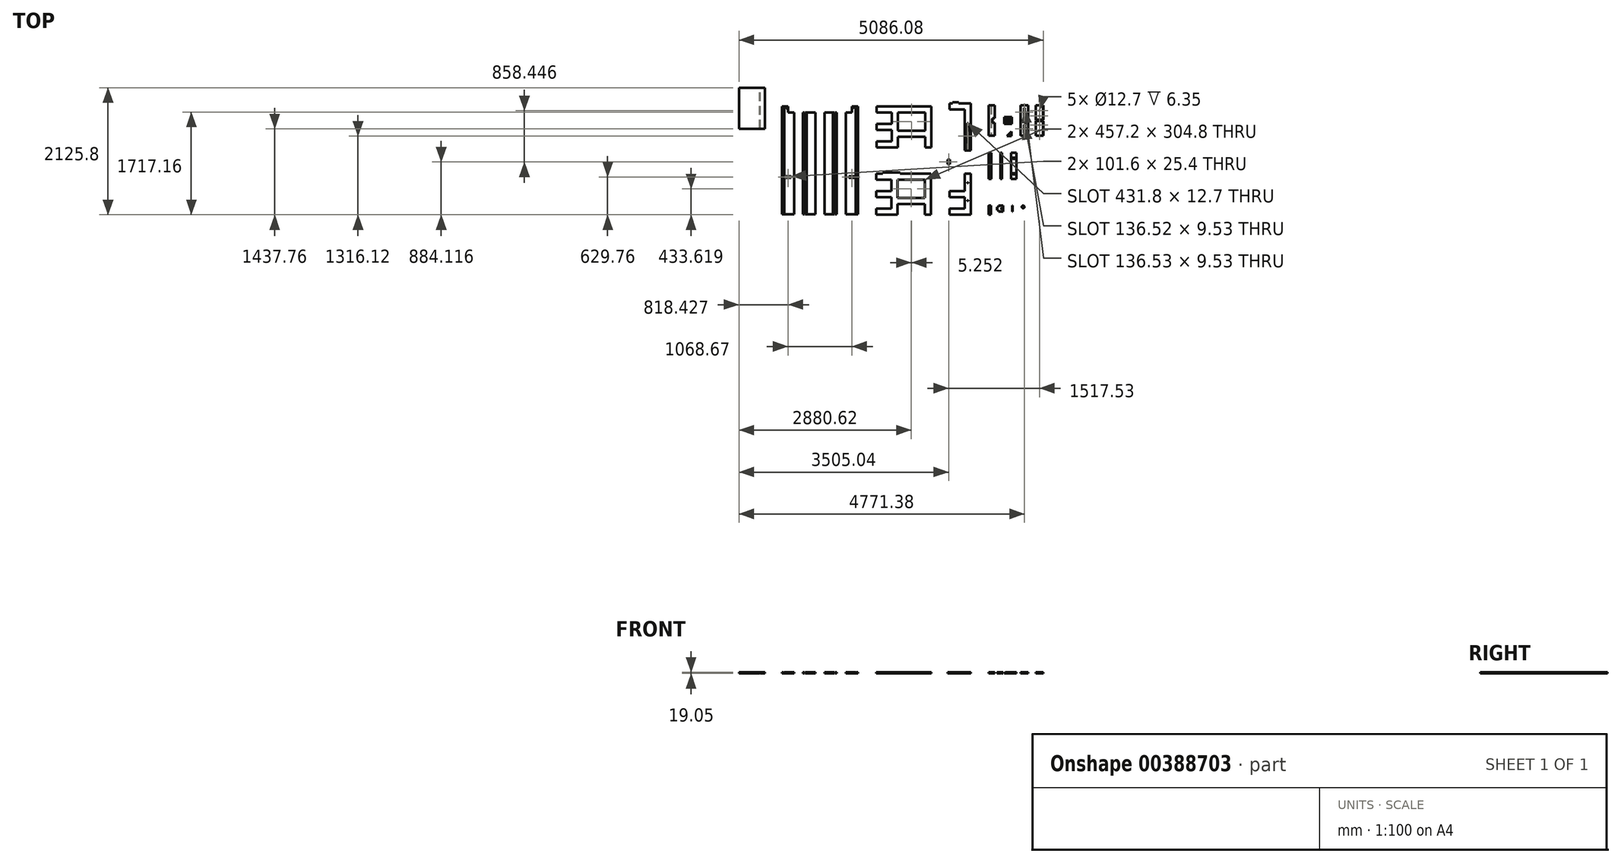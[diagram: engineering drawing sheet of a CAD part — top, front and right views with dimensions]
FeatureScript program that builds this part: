
annotation { "Feature Type Name" : "Feature", "Feature Type Description" : "" }
export const myFeature = defineFeature(function(context is Context, id is Id, definition is map)
    precondition{}
    {
        {
            var Q0;
            Q0=qCreatedBy(makeId("Top.planeOp"),FACE);
            var sketch = newSketch(context, id + "F0", { "sketchPlane" : qUnion([Q0])});
            skLineSegment(sketch, "E0.bottom", {"start": v(-431.8, 0) * mm, "end": v(0, 0) * mm});
            skLineSegment(sketch, "E0.top", {"start": v(-431.8, -685.8) * mm, "end": v(0, -685.8) * mm});
            skLineSegment(sketch, "E0.left", {"start": v(-431.8, 0) * mm, "end": v(-431.8, -685.8) * mm});
            skLineSegment(sketch, "E0.right", {"start": v(0, 0) * mm, "end": v(0, -685.8) * mm});
            skLineSegment(sketch, "E1", {"start": v(1869.87, -315.68) * mm, "end": v(2784.27, -315.68) * mm});
            skLineSegment(sketch, "E2", {"start": v(2784.27, -315.68) * mm, "end": v(2784.27, -1001.48) * mm});
            skLineSegment(sketch, "E3", {"start": v(2784.27, -1001.48) * mm, "end": v(2682.67, -1001.48) * mm});
            skLineSegment(sketch, "E4", {"start": v(2682.67, -1001.48) * mm, "end": v(2682.67, -823.68) * mm});
            skLineSegment(sketch, "E5", {"start": v(2682.67, -823.68) * mm, "end": v(2225.47, -823.68) * mm});
            skLineSegment(sketch, "E6", {"start": v(2225.47, -823.68) * mm, "end": v(2225.47, -1001.48) * mm});
            skLineSegment(sketch, "E7", {"start": v(2225.47, -1001.48) * mm, "end": v(1869.87, -1001.48) * mm});
            skLineSegment(sketch, "E8", {"start": v(1869.87, -1001.48) * mm, "end": v(1869.87, -899.88) * mm});
            skLineSegment(sketch, "E9", {"start": v(1869.87, -899.88) * mm, "end": v(2123.87, -899.88) * mm});
            skLineSegment(sketch, "E10", {"start": v(2123.87, -899.88) * mm, "end": v(2123.87, -709.38) * mm});
            skLineSegment(sketch, "E11", {"start": v(2123.87, -709.38) * mm, "end": v(1869.87, -709.38) * mm});
            skLineSegment(sketch, "E12", {"start": v(1869.87, -709.38) * mm, "end": v(1869.87, -607.78) * mm});
            skLineSegment(sketch, "E13", {"start": v(1869.87, -607.78) * mm, "end": v(2123.87, -607.78) * mm});
            skLineSegment(sketch, "E14", {"start": v(2123.87, -607.78) * mm, "end": v(2123.87, -417.28) * mm});
            skLineSegment(sketch, "E15", {"start": v(2123.87, -417.28) * mm, "end": v(1869.87, -417.28) * mm});
            skLineSegment(sketch, "E16", {"start": v(1869.87, -417.28) * mm, "end": v(1869.87, -315.68) * mm});
            skLineSegment(sketch, "E17.bottom", {"start": v(2225.47, -417.28) * mm, "end": v(2682.67, -417.28) * mm});
            skLineSegment(sketch, "E17.top", {"start": v(2225.47, -722.08) * mm, "end": v(2682.67, -722.08) * mm});
            skLineSegment(sketch, "E17.left", {"start": v(2225.47, -417.28) * mm, "end": v(2225.47, -722.08) * mm});
            skLineSegment(sketch, "E17.right", {"start": v(2682.67, -417.28) * mm, "end": v(2682.67, -722.08) * mm});
            skLineSegment(sketch, "E18", {"start": v(1864.62, -1438.18) * mm, "end": v(1972.57, -1438.18) * mm});
            skLineSegment(sketch, "E19", {"start": v(2779.02, -1438.18) * mm, "end": v(2779.02, -2123.98) * mm});
            skLineSegment(sketch, "E20", {"start": v(2779.02, -2123.98) * mm, "end": v(2677.42, -2123.98) * mm});
            skLineSegment(sketch, "E21", {"start": v(2677.42, -2123.98) * mm, "end": v(2677.42, -1946.18) * mm});
            skLineSegment(sketch, "E22", {"start": v(2677.42, -1946.18) * mm, "end": v(2220.22, -1946.18) * mm});
            skLineSegment(sketch, "E23", {"start": v(2220.22, -1946.18) * mm, "end": v(2220.22, -2123.98) * mm});
            skLineSegment(sketch, "E24", {"start": v(2220.22, -2123.98) * mm, "end": v(1864.62, -2123.98) * mm});
            skLineSegment(sketch, "E25", {"start": v(1864.62, -2123.98) * mm, "end": v(1864.62, -2022.38) * mm});
            skLineSegment(sketch, "E26", {"start": v(1864.62, -2022.38) * mm, "end": v(2118.62, -2022.38) * mm});
            skLineSegment(sketch, "E27", {"start": v(2118.62, -2022.38) * mm, "end": v(2118.62, -1831.88) * mm});
            skLineSegment(sketch, "E28", {"start": v(2118.62, -1831.88) * mm, "end": v(1864.62, -1831.88) * mm});
            skLineSegment(sketch, "E29", {"start": v(1864.62, -1831.88) * mm, "end": v(1864.62, -1730.28) * mm});
            skLineSegment(sketch, "E30", {"start": v(1864.62, -1730.28) * mm, "end": v(2118.62, -1730.28) * mm});
            skLineSegment(sketch, "E31", {"start": v(2118.62, -1730.28) * mm, "end": v(2118.62, -1539.78) * mm});
            skLineSegment(sketch, "E32", {"start": v(2118.62, -1539.78) * mm, "end": v(1864.62, -1539.78) * mm});
            skLineSegment(sketch, "E33", {"start": v(1864.62, -1539.78) * mm, "end": v(1864.62, -1438.18) * mm});
            skLineSegment(sketch, "E34.bottom", {"start": v(2220.22, -1539.78) * mm, "end": v(2677.42, -1539.78) * mm});
            skLineSegment(sketch, "E34.top", {"start": v(2220.22, -1844.58) * mm, "end": v(2677.42, -1844.58) * mm});
            skLineSegment(sketch, "E34.left", {"start": v(2220.22, -1539.78) * mm, "end": v(2220.22, -1844.58) * mm});
            skLineSegment(sketch, "E34.right", {"start": v(2677.42, -1539.78) * mm, "end": v(2677.42, -1844.58) * mm});
            skLineSegment(sketch, "E35", {"start": v(1972.57, -1438.18) * mm, "end": v(1972.57, -1419.13) * mm});
            skLineSegment(sketch, "E36", {"start": v(1972.57, -1419.13) * mm, "end": v(2264.67, -1419.13) * mm});
            skLineSegment(sketch, "E37", {"start": v(2264.67, -1419.13) * mm, "end": v(2264.67, -1438.18) * mm});
            skLineSegment(sketch, "E38.trimOffspring", {"start": v(2264.67, -1438.18) * mm, "end": v(2779.02, -1438.18) * mm});
            skLineSegment(sketch, "E39", {"start": v(3088.07, -263.58) * mm, "end": v(3138.87, -263.58) * mm});
            skLineSegment(sketch, "E40", {"start": v(3138.87, -263.58) * mm, "end": v(3138.87, -244.53) * mm});
            skLineSegment(sketch, "E41", {"start": v(3138.87, -244.53) * mm, "end": v(3240.47, -244.53) * mm});
            skLineSegment(sketch, "E42", {"start": v(3240.47, -244.53) * mm, "end": v(3240.47, -263.58) * mm});
            skLineSegment(sketch, "E43", {"start": v(3240.47, -263.58) * mm, "end": v(3443.67, -263.58) * mm});
            skLineSegment(sketch, "E44", {"start": v(3443.67, -263.58) * mm, "end": v(3443.67, -1050.98) * mm});
            skLineSegment(sketch, "E45", {"start": v(3443.67, -1050.98) * mm, "end": v(3342.07, -1050.98) * mm});
            skLineSegment(sketch, "E46", {"start": v(3342.07, -1050.98) * mm, "end": v(3342.07, -365.18) * mm});
            skLineSegment(sketch, "E47", {"start": v(3342.07, -365.18) * mm, "end": v(3088.07, -365.18) * mm});
            skLineSegment(sketch, "E48", {"start": v(3088.07, -365.18) * mm, "end": v(3088.07, -263.58) * mm});
            skLineSegment(sketch, "E49.bottom", {"start": v(3392.87, -593.78) * mm, "end": v(3392.87, -593.78) * mm});
            skLineSegment(sketch, "E49.top", {"start": v(3392.87, -1025.58) * mm, "end": v(3392.87, -1025.58) * mm});
            skLineSegment(sketch, "E49.left", {"start": v(3386.52, -600.13) * mm, "end": v(3386.52, -1019.23) * mm});
            skLineSegment(sketch, "E49.right", {"start": v(3399.22, -600.13) * mm, "end": v(3399.22, -1019.23) * mm});
            skLineSegment(sketch, "E50", {"start": v(3392.87, -593.78) * mm, "end": v(3392.87, -1025.58) * mm, "construction": true});
            skPoint(sketch, "E51.visualSharp", {"position": v(3386.52, -593.78) * mm});
            skArc(sketch, "E51.filletArc", {"start": v(3392.87, -593.78) * mm, "mid": v(3388.38, -595.64) * mm, "end": v(3386.52, -600.13) * mm});
            skPoint(sketch, "E52.visualSharp", {"position": v(3399.22, -593.78) * mm});
            skArc(sketch, "E52.filletArc", {"start": v(3399.22, -600.13) * mm, "mid": v(3397.36, -595.64) * mm, "end": v(3392.87, -593.78) * mm});
            skPoint(sketch, "E53.visualSharp", {"position": v(3386.52, -1025.58) * mm});
            skArc(sketch, "E53.filletArc", {"start": v(3386.52, -1019.23) * mm, "mid": v(3388.38, -1023.72) * mm, "end": v(3392.87, -1025.58) * mm});
            skPoint(sketch, "E54.visualSharp", {"position": v(3399.22, -1025.58) * mm});
            skArc(sketch, "E54.filletArc", {"start": v(3392.87, -1025.58) * mm, "mid": v(3397.36, -1023.72) * mm, "end": v(3399.22, -1019.23) * mm});
            skLineSegment(sketch, "E55", {"start": v(3443.67, -1437.84) * mm, "end": v(3443.67, -2123.64) * mm});
            skLineSegment(sketch, "E56", {"start": v(3443.67, -2123.64) * mm, "end": v(3088.07, -2123.64) * mm});
            skLineSegment(sketch, "E57", {"start": v(3088.07, -2123.64) * mm, "end": v(3088.07, -2022.04) * mm});
            skLineSegment(sketch, "E58", {"start": v(3088.07, -2022.04) * mm, "end": v(3342.07, -2022.04) * mm});
            skLineSegment(sketch, "E59", {"start": v(3342.07, -2022.04) * mm, "end": v(3342.07, -1831.54) * mm});
            skLineSegment(sketch, "E60", {"start": v(3342.07, -1831.54) * mm, "end": v(3088.07, -1831.54) * mm});
            skLineSegment(sketch, "E61", {"start": v(3088.07, -1831.54) * mm, "end": v(3088.07, -1729.94) * mm});
            skLineSegment(sketch, "E62", {"start": v(3088.07, -1729.94) * mm, "end": v(3342.07, -1729.94) * mm});
            skLineSegment(sketch, "E63", {"start": v(3342.07, -1729.94) * mm, "end": v(3342.07, -1437.84) * mm});
            skLineSegment(sketch, "E64", {"start": v(3342.07, -1437.84) * mm, "end": v(3443.67, -1437.84) * mm});
            skCircle(sketch, "E65", {"center": v(3392.87, -1590.24) * mm, "radius": 6.35 * mm});
            skCircle(sketch, "E66", {"center": v(3392.87, -1888.69) * mm, "radius": 6.35 * mm});
            skLineSegment(sketch, "E67.bottom", {"start": v(285.23, -314.94) * mm, "end": v(386.83, -314.94) * mm});
            skLineSegment(sketch, "E67.top", {"start": v(285.23, -2118.34) * mm, "end": v(488.43, -2118.34) * mm});
            skLineSegment(sketch, "E67.left", {"start": v(285.23, -314.94) * mm, "end": v(285.23, -2118.34) * mm});
            skLineSegment(sketch, "E67.right", {"start": v(488.43, -416.54) * mm, "end": v(488.43, -2118.34) * mm});
            skLineSegment(sketch, "E68", {"start": v(488.43, -416.54) * mm, "end": v(386.83, -416.54) * mm});
            skPoint(sketch, "E68.endSnap0", {"position": v(386.83, -314.94) * mm});
            skLineSegment(sketch, "E69", {"start": v(386.83, -416.54) * mm, "end": v(386.83, -314.94) * mm});
            skLineSegment(sketch, "E70", {"start": v(920.96, -314.94) * mm, "end": v(920.96, -2118.34) * mm, "construction": true});
            skLineSegment(sketch, "E71.bottom", {"start": v(335.83, -1483.34) * mm, "end": v(437.43, -1483.34) * mm});
            skLineSegment(sketch, "E71.top", {"start": v(335.83, -1508.74) * mm, "end": v(437.43, -1508.74) * mm});
            skLineSegment(sketch, "E71.left", {"start": v(335.83, -1483.34) * mm, "end": v(335.83, -1508.74) * mm});
            skLineSegment(sketch, "E71.right", {"start": v(437.43, -1483.34) * mm, "end": v(437.43, -1508.74) * mm});
            skLineSegment(sketch, "E72", {"start": v(335.83, -1496.04) * mm, "end": v(437.43, -1496.04) * mm, "construction": true});
            skCircle(sketch, "E73", {"center": v(374.13, -343.52) * mm, "radius": 9.53 * mm});
            skLineSegment(sketch, "E74.bottom", {"start": v(639.73, -416.54) * mm, "end": v(844.76, -416.54) * mm});
            skLineSegment(sketch, "E74.top", {"start": v(639.73, -2118.34) * mm, "end": v(844.76, -2118.34) * mm});
            skLineSegment(sketch, "E74.left", {"start": v(639.73, -416.54) * mm, "end": v(639.73, -2118.34) * mm});
            skLineSegment(sketch, "E74.right", {"start": v(844.76, -416.54) * mm, "end": v(844.76, -2118.34) * mm});
            skLineSegment(sketch, "E75.MirrorCS", {"start": v(1506.1, -1483.34) * mm, "end": v(1506.1, -1508.74) * mm});
            skLineSegment(sketch, "E76.MirrorCS", {"start": v(1404.5, -1483.34) * mm, "end": v(1404.5, -1508.74) * mm});
            skCircle(sketch, "E77.MirrorC", {"center": v(1467.79, -343.52) * mm, "radius": 9.53 * mm});
            skLineSegment(sketch, "E78.MirrorCS", {"start": v(1455.09, -416.54) * mm, "end": v(1455.09, -314.94) * mm});
            skLineSegment(sketch, "E79.MirrorCS", {"start": v(1202.2, -416.54) * mm, "end": v(1202.2, -2118.34) * mm});
            skLineSegment(sketch, "E80.MirrorCS", {"start": v(1506.1, -1483.34) * mm, "end": v(1404.5, -1483.34) * mm});
            skLineSegment(sketch, "E81.MirrorCS", {"start": v(997.16, -416.54) * mm, "end": v(997.16, -2118.34) * mm});
            skLineSegment(sketch, "E82.MirrorCS", {"start": v(1506.1, -1508.74) * mm, "end": v(1404.5, -1508.74) * mm});
            skLineSegment(sketch, "E83.MirrorCS", {"start": v(1556.69, -2118.34) * mm, "end": v(1353.49, -2118.34) * mm});
            skLineSegment(sketch, "E84.MirrorCS", {"start": v(1556.69, -314.94) * mm, "end": v(1556.69, -2118.34) * mm});
            skLineSegment(sketch, "E85.MirrorCS", {"start": v(1353.49, -416.54) * mm, "end": v(1353.49, -2118.34) * mm});
            skPoint(sketch, "E86.MirrorP", {"position": v(1455.09, -314.94) * mm});
            skLineSegment(sketch, "E87.MirrorCS", {"start": v(1556.69, -314.94) * mm, "end": v(1455.09, -314.94) * mm});
            skLineSegment(sketch, "E88.MirrorCS", {"start": v(1506.1, -1496.04) * mm, "end": v(1404.5, -1496.04) * mm, "construction": true});
            skLineSegment(sketch, "E89.MirrorCS", {"start": v(1202.2, -416.54) * mm, "end": v(997.16, -416.54) * mm});
            skLineSegment(sketch, "E90.MirrorCS", {"start": v(1353.49, -416.54) * mm, "end": v(1455.09, -416.54) * mm});
            skLineSegment(sketch, "E91.MirrorCS", {"start": v(1202.2, -2118.34) * mm, "end": v(997.16, -2118.34) * mm});
            skLineSegment(sketch, "E92.bottom", {"start": v(3054.2, -1203.58) * mm, "end": v(3092.3, -1203.58) * mm});
            skLineSegment(sketch, "E92.top", {"start": v(3054.2, -1279.78) * mm, "end": v(3092.3, -1279.78) * mm});
            skLineSegment(sketch, "E92.left", {"start": v(3054.2, -1203.58) * mm, "end": v(3054.2, -1279.78) * mm});
            skLineSegment(sketch, "E92.right", {"start": v(3092.3, -1203.58) * mm, "end": v(3092.3, -1279.78) * mm});
            skCircle(sketch, "E93", {"center": v(3073.24, -1241.68) * mm, "radius": 4.76 * mm});
            skLineSegment(sketch, "E94.bottom", {"start": v(3743.01, -294.34) * mm, "end": v(3845.7, -294.34) * mm});
            skLineSegment(sketch, "E94.top", {"start": v(3743.01, -802.34) * mm, "end": v(3845.7, -802.34) * mm});
            skLineSegment(sketch, "E94.left", {"start": v(3743.01, -294.34) * mm, "end": v(3743.01, -802.34) * mm});
            skLineSegment(sketch, "E94.right", {"start": v(3845.7, -294.34) * mm, "end": v(3845.7, -510.24) * mm});
            skLineSegment(sketch, "E95.bottom", {"start": v(4003.93, -492.95) * mm, "end": v(4130.93, -492.95) * mm});
            skLineSegment(sketch, "E95.top", {"start": v(4003.93, -607.25) * mm, "end": v(4130.93, -607.25) * mm});
            skLineSegment(sketch, "E95.left", {"start": v(4003.93, -492.95) * mm, "end": v(4003.93, -607.25) * mm});
            skLineSegment(sketch, "E95.right", {"start": v(4130.93, -492.95) * mm, "end": v(4130.93, -607.25) * mm});
            skLineSegment(sketch, "E96.bottom", {"start": v(4276.08, -294.34) * mm, "end": v(4403.08, -294.34) * mm});
            skLineSegment(sketch, "E96.top", {"start": v(4276.08, -802.34) * mm, "end": v(4403.08, -802.34) * mm});
            skLineSegment(sketch, "E96.left", {"start": v(4276.08, -294.34) * mm, "end": v(4276.08, -802.34) * mm});
            skLineSegment(sketch, "E96.right", {"start": v(4403.08, -294.34) * mm, "end": v(4403.08, -512.12) * mm});
            skLineSegment(sketch, "E97.bottom", {"start": v(4527.28, -294.34) * mm, "end": v(4654.28, -294.34) * mm});
            skLineSegment(sketch, "E97.top", {"start": v(4527.28, -541.99) * mm, "end": v(4651.1, -541.99) * mm});
            skLineSegment(sketch, "E97.left", {"start": v(4527.28, -294.34) * mm, "end": v(4527.28, -541.99) * mm});
            skLineSegment(sketch, "E97.right", {"start": v(4654.28, -294.34) * mm, "end": v(4654.28, -538.81) * mm});
            skLineSegment(sketch, "E98.bottom", {"start": v(3743.16, -1090.23) * mm, "end": v(3787.6, -1090.23) * mm});
            skLineSegment(sketch, "E98.top", {"start": v(3743.16, -1528.38) * mm, "end": v(3787.6, -1528.38) * mm});
            skLineSegment(sketch, "E98.left", {"start": v(3743.16, -1090.23) * mm, "end": v(3743.16, -1528.38) * mm});
            skLineSegment(sketch, "E98.right", {"start": v(3787.6, -1090.23) * mm, "end": v(3787.6, -1528.38) * mm});
            skLineSegment(sketch, "E99.bottom", {"start": v(3940.76, -1090.23) * mm, "end": v(3966.16, -1090.23) * mm});
            skLineSegment(sketch, "E99.top", {"start": v(3940.76, -1528.38) * mm, "end": v(3966.16, -1528.38) * mm});
            skLineSegment(sketch, "E99.left", {"start": v(3940.76, -1090.23) * mm, "end": v(3940.76, -1528.38) * mm});
            skLineSegment(sketch, "E99.right", {"start": v(3966.16, -1090.23) * mm, "end": v(3966.16, -1528.38) * mm});
            skLineSegment(sketch, "E100.bottom", {"start": v(4118.5, -1090.23) * mm, "end": v(4207.4, -1090.23) * mm});
            skLineSegment(sketch, "E100.top", {"start": v(4118.5, -1528.38) * mm, "end": v(4207.4, -1528.38) * mm});
            skLineSegment(sketch, "E100.left", {"start": v(4118.5, -1090.23) * mm, "end": v(4118.5, -1528.38) * mm});
            skLineSegment(sketch, "E100.right", {"start": v(4207.4, -1090.23) * mm, "end": v(4207.4, -1528.38) * mm});
            skLineSegment(sketch, "E101.bottom", {"start": v(3778.37, -1973.4) * mm, "end": v(3746.62, -1973.4) * mm});
            skLineSegment(sketch, "E101.top", {"start": v(3778.37, -2125.8) * mm, "end": v(3743.45, -2125.8) * mm});
            skLineSegment(sketch, "E101.left", {"start": v(3778.37, -1973.4) * mm, "end": v(3778.37, -2125.8) * mm});
            skLineSegment(sketch, "E101.right", {"start": v(3740.27, -1979.75) * mm, "end": v(3740.27, -2049.6) * mm});
            skLineSegment(sketch, "E102.bottom", {"start": v(3982.85, -1971.8) * mm, "end": v(3906.65, -1971.8) * mm});
            skLineSegment(sketch, "E102.top", {"start": v(3982.85, -2073.4) * mm, "end": v(3906.65, -2073.4) * mm});
            skLineSegment(sketch, "E102.left", {"start": v(3982.85, -1971.8) * mm, "end": v(3982.85, -2073.4) * mm});
            skLineSegment(sketch, "E102.right", {"start": v(3881.25, -1997.2) * mm, "end": v(3881.25, -2048) * mm});
            skLineSegment(sketch, "E103.bottom", {"start": v(4136.98, -1971.3) * mm, "end": v(4144.92, -1971.3) * mm});
            skLineSegment(sketch, "E103.top", {"start": v(4136.98, -2072.9) * mm, "end": v(4144.92, -2072.9) * mm});
            skLineSegment(sketch, "E103.left", {"start": v(4136.98, -1971.3) * mm, "end": v(4136.98, -2072.9) * mm});
            skLineSegment(sketch, "E103.right", {"start": v(4144.92, -1971.3) * mm, "end": v(4144.92, -2072.9) * mm});
            skCircle(sketch, "E104", {"center": v(4318.4, -1993.53) * mm, "radius": 22.23 * mm});
            skLineSegment(sketch, "E105", {"start": v(3845.7, -510.24) * mm, "end": v(3804.22, -510.24) * mm});
            skLineSegment(sketch, "E106", {"start": v(3804.22, -510.24) * mm, "end": v(3804.22, -586.44) * mm});
            skLineSegment(sketch, "E107", {"start": v(3804.22, -586.44) * mm, "end": v(3845.7, -586.44) * mm});
            skLineSegment(sketch, "E108.trimOffspring", {"start": v(3845.7, -586.44) * mm, "end": v(3845.7, -802.34) * mm});
            skCircle(sketch, "E109", {"center": v(4067.43, -550.1) * mm, "radius": 22.23 * mm});
            skPoint(sketch, "E109.centerSnap0", {"position": v(4003.93, -550.1) * mm});
            skPoint(sketch, "E109.centerSnap1", {"position": v(4067.43, -492.95) * mm});
            skLineSegment(sketch, "E110", {"start": v(4123.85, -732.63) * mm, "end": v(4123.85, -808.83) * mm});
            skLineSegment(sketch, "E111", {"start": v(4123.85, -808.83) * mm, "end": v(4047.65, -808.83) * mm});
            skLineSegment(sketch, "E112", {"start": v(4047.65, -808.83) * mm, "end": v(4123.85, -732.63) * mm});
            skLineSegment(sketch, "E113", {"start": v(4403.08, -512.12) * mm, "end": v(4352.28, -512.12) * mm});
            skLineSegment(sketch, "E114", {"start": v(4352.28, -512.12) * mm, "end": v(4352.28, -588.32) * mm});
            skLineSegment(sketch, "E115", {"start": v(4352.28, -588.32) * mm, "end": v(4403.08, -588.32) * mm});
            skLineSegment(sketch, "E116.trimOffspring", {"start": v(4403.08, -588.32) * mm, "end": v(4403.08, -802.34) * mm});
            skLineSegment(sketch, "E117", {"start": v(4654.28, -538.81) * mm, "end": v(4651.1, -541.99) * mm});
            skLineSegment(sketch, "E118", {"start": v(4339.58, -294.34) * mm, "end": v(4339.58, -802.34) * mm, "construction": true});
            skLineSegment(sketch, "E119", {"start": v(4339.58, -751.54) * mm, "end": v(4339.58, -624.54) * mm});
            skLineSegment(sketch, "E120", {"start": v(4339.58, -472.14) * mm, "end": v(4339.58, -345.14) * mm});
            skArc(sketch, "E121.0.startCap", {"start": v(4344.34, -751.54) * mm, "mid": v(4339.58, -756.3) * mm, "end": v(4334.82, -751.54) * mm});
            skArc(sketch, "E121.0.endCap", {"start": v(4334.82, -624.54) * mm, "mid": v(4339.58, -619.77) * mm, "end": v(4344.34, -624.54) * mm});
            skLineSegment(sketch, "E121.0.left", {"start": v(4334.82, -751.54) * mm, "end": v(4334.82, -624.54) * mm});
            skLineSegment(sketch, "E121.0.right", {"start": v(4344.34, -751.54) * mm, "end": v(4344.34, -624.54) * mm});
            skArc(sketch, "E122.0.startCap", {"start": v(4344.34, -472.14) * mm, "mid": v(4339.58, -476.9) * mm, "end": v(4334.82, -472.14) * mm});
            skArc(sketch, "E122.0.endCap", {"start": v(4334.82, -345.14) * mm, "mid": v(4339.58, -340.37) * mm, "end": v(4344.34, -345.14) * mm});
            skLineSegment(sketch, "E122.0.left", {"start": v(4334.82, -472.14) * mm, "end": v(4334.82, -345.14) * mm});
            skLineSegment(sketch, "E122.0.right", {"start": v(4344.34, -472.14) * mm, "end": v(4344.34, -345.14) * mm});
            skLineSegment(sketch, "E123", {"start": v(4527.28, -548.34) * mm, "end": v(4654.28, -548.34) * mm, "construction": true});
            skLineSegment(sketch, "E124", {"start": v(4590.78, -294.34) * mm, "end": v(4590.78, -541.99) * mm, "construction": true});
            skPoint(sketch, "E124.endSnap0", {"position": v(4589.19, -541.99) * mm});
            skCircle(sketch, "E125", {"center": v(4590.78, -472.14) * mm, "radius": 3.97 * mm});
            skCircle(sketch, "E126", {"center": v(4590.78, -383.24) * mm, "radius": 3.97 * mm});
            skLineSegment(sketch, "E127.MirrorCS", {"start": v(4654.28, -557.86) * mm, "end": v(4651.1, -554.69) * mm});
            skLineSegment(sketch, "E128.MirrorCS", {"start": v(4527.28, -554.69) * mm, "end": v(4651.1, -554.69) * mm});
            skCircle(sketch, "E129.MirrorC", {"center": v(4590.78, -713.44) * mm, "radius": 3.97 * mm});
            skCircle(sketch, "E130.MirrorC", {"center": v(4590.78, -624.54) * mm, "radius": 3.97 * mm});
            skPoint(sketch, "E131.MirrorP", {"position": v(4589.19, -554.69) * mm});
            skLineSegment(sketch, "E132.MirrorCS", {"start": v(4527.28, -802.34) * mm, "end": v(4654.28, -802.34) * mm});
            skLineSegment(sketch, "E133.MirrorCS", {"start": v(4527.28, -802.34) * mm, "end": v(4527.28, -554.69) * mm});
            skLineSegment(sketch, "E134.MirrorCS", {"start": v(4654.28, -802.34) * mm, "end": v(4654.28, -557.86) * mm});
            skLineSegment(sketch, "E135.MirrorCS", {"start": v(4590.78, -802.34) * mm, "end": v(4590.78, -554.69) * mm, "construction": true});
            skLineSegment(sketch, "E136", {"start": v(4118.5, -1309.3) * mm, "end": v(4207.4, -1309.3) * mm, "construction": true});
            skLineSegment(sketch, "E137", {"start": v(4152.47, -1179.13) * mm, "end": v(4173.41, -1179.13) * mm, "construction": true});
            skLineSegment(sketch, "E138", {"start": v(4162.94, -1090.23) * mm, "end": v(4162.94, -1528.38) * mm, "construction": true});
            skPoint(sketch, "E139", {"position": v(4162.94, -1179.13) * mm});
            skArc(sketch, "E140.0.startCap", {"start": v(4152.47, -1183.89) * mm, "mid": v(4147.7, -1179.13) * mm, "end": v(4152.47, -1174.36) * mm});
            skArc(sketch, "E140.0.endCap", {"start": v(4173.41, -1174.36) * mm, "mid": v(4178.17, -1179.13) * mm, "end": v(4173.41, -1183.89) * mm});
            skLineSegment(sketch, "E140.0.left", {"start": v(4152.47, -1174.36) * mm, "end": v(4173.41, -1174.36) * mm});
            skLineSegment(sketch, "E140.0.right", {"start": v(4152.47, -1183.89) * mm, "end": v(4173.41, -1183.89) * mm});
            skArc(sketch, "E141.MirrorCS", {"start": v(4173.41, -1444.24) * mm, "mid": v(4178.17, -1439.48) * mm, "end": v(4173.41, -1434.71) * mm});
            skLineSegment(sketch, "E142.MirrorCS", {"start": v(4152.47, -1434.71) * mm, "end": v(4173.41, -1434.71) * mm});
            skPoint(sketch, "E143.MirrorP", {"position": v(4162.94, -1439.48) * mm});
            skLineSegment(sketch, "E144.MirrorCS", {"start": v(4152.47, -1439.48) * mm, "end": v(4173.41, -1439.48) * mm, "construction": true});
            skLineSegment(sketch, "E145.MirrorCS", {"start": v(4152.47, -1444.24) * mm, "end": v(4173.41, -1444.24) * mm});
            skArc(sketch, "E146.MirrorCS", {"start": v(4152.47, -1434.71) * mm, "mid": v(4147.7, -1439.48) * mm, "end": v(4152.47, -1444.24) * mm});
            skCircle(sketch, "E147", {"center": v(4318.4, -1993.53) * mm, "radius": 4.76 * mm});
            skLineSegment(sketch, "E148", {"start": v(3906.65, -1971.8) * mm, "end": v(3906.65, -1997.2) * mm});
            skLineSegment(sketch, "E149", {"start": v(3906.65, -1997.2) * mm, "end": v(3881.25, -1997.2) * mm});
            skLineSegment(sketch, "E150", {"start": v(3881.25, -2048) * mm, "end": v(3906.65, -2048) * mm});
            skLineSegment(sketch, "E151", {"start": v(3906.65, -2048) * mm, "end": v(3906.65, -2073.4) * mm});
            skCircle(sketch, "E152", {"center": v(3952.68, -2022.6) * mm, "radius": 3.18 * mm});
            skLineSegment(sketch, "E153", {"start": v(3881.25, -2022.6) * mm, "end": v(3982.85, -2022.6) * mm, "construction": true});
            skCircle(sketch, "E154", {"center": v(3748.21, -1986.1) * mm, "radius": 3.18 * mm});
            skPoint(sketch, "E155.visualSharp", {"position": v(3740.27, -1973.4) * mm});
            skArc(sketch, "E155.filletArc", {"start": v(3746.62, -1973.4) * mm, "mid": v(3742.13, -1975.26) * mm, "end": v(3740.27, -1979.75) * mm});
            skLineSegment(sketch, "E156", {"start": v(3740.27, -2049.6) * mm, "end": v(3740.27, -2049.6) * mm});
            skLineSegment(sketch, "E157", {"start": v(3743.45, -2049.6) * mm, "end": v(3743.45, -2125.8) * mm});
            skLineSegment(sketch, "E158", {"start": v(3740.27, -2049.6) * mm, "end": v(3743.45, -2049.6) * mm});
            skCircle(sketch, "E159", {"center": v(4140.95, -2022.1) * mm, "radius": 3.18 * mm});
            skPoint(sketch, "E159.centerSnap0", {"position": v(4136.98, -2022.1) * mm});
            skPoint(sketch, "E159.centerSnap1", {"position": v(4140.95, -1971.3) * mm});
            skSolve(sketch);
        }
        {
            var Q0;
            Q0 = qSketchRegion(id + "F0", true);
            extrude(context, id + "F1", {"entities" : qUnion([Q0]), "depth" : 19.05 * mm});
        }
        {
            var Q0;
            Q0=makeQuery(id+"F1.opExtrude","CAP_FACE",FACE,{"disambiguationData":[OSD([sQuery(id+"F0.wireOp",EDGE,"E0.bottom"),sQuery(id+"F0.wireOp",EDGE,"E0.top"),sQuery(id+"F0.wireOp",EDGE,"E0.left"),sQuery(id+"F0.wireOp",EDGE,"E0.right")])],"isStart":true});
            var sketch = newSketch(context, id + "F2", { "sketchPlane" : qUnion([Q0])});
            skLineSegment(sketch, "E160.bottom", {"start": v(-88.9, 685.8) * mm, "end": v(-76.2, 685.8) * mm});
            skLineSegment(sketch, "E160.top", {"start": v(-88.9, 0) * mm, "end": v(-76.2, 0) * mm});
            skLineSegment(sketch, "E160.left", {"start": v(-88.9, 685.8) * mm, "end": v(-88.9, 0) * mm});
            skLineSegment(sketch, "E160.right", {"start": v(-76.2, 685.8) * mm, "end": v(-76.2, 0) * mm});
            skSolve(sketch);
        }
        {
            var Q0;
            Q0 = qSketchRegion(id + "F2", true);
            extrude(context, id + "F3", {"entities" : qUnion([Q0]), "operationType" : NewBodyOperationType.REMOVE, "oppositeDirection" : true, "depth" : 6.35 * mm});
        }
        {
            var Q0;
            Q0=makeQuery(id+"F1.opExtrude","SWEPT_FACE",FACE,{"disambiguationData":[OSD([sQuery(id+"F0.wireOp",EDGE,"E67.top")])]});
            var sketch = newSketch(context, id + "F4", { "sketchPlane" : qUnion([Q0])});
            skLineSegment(sketch, "E161.bottom", {"start": v(307.46, 19.05) * mm, "end": v(323.33, 19.05) * mm});
            skLineSegment(sketch, "E161.top", {"start": v(307.46, 12.7) * mm, "end": v(323.33, 12.7) * mm});
            skLineSegment(sketch, "E161.left", {"start": v(307.46, 19.05) * mm, "end": v(307.46, 12.7) * mm});
            skLineSegment(sketch, "E161.right", {"start": v(323.33, 19.05) * mm, "end": v(323.33, 12.7) * mm});
            skPoint(sketch, "E162.orphan", {"position": v(844.76, 19.05) * mm});
            skSolve(sketch);
        }
        {
            var Q0;
            Q0 = qSketchRegion(id + "F4", true);
            extrude(context, id + "F5", {"entities" : qUnion([Q0]), "operationType" : NewBodyOperationType.REMOVE, "endBound" : BoundingType.THROUGH_ALL, "oppositeDirection" : true, "depth" : 25.4 * mm});
        }
        {
            var Q0;
            Q0=makeQuery(id+"F1.opExtrude","SWEPT_FACE",FACE,{"disambiguationData":[OSD([sQuery(id+"F0.wireOp",EDGE,"E74.top")])]});
            var sketch = newSketch(context, id + "F6", { "sketchPlane" : qUnion([Q0])});
            skLineSegment(sketch, "E163", {"start": v(639.73, 19.05) * mm, "end": v(639.73, 17.46) * mm});
            skLineSegment(sketch, "E164", {"start": v(639.73, 17.46) * mm, "end": v(665.13, 17.46) * mm});
            skLineSegment(sketch, "E165", {"start": v(665.13, 17.46) * mm, "end": v(665.13, 0) * mm});
            skLineSegment(sketch, "E166", {"start": v(665.13, 0) * mm, "end": v(674.65, 0) * mm});
            skLineSegment(sketch, "E167", {"start": v(674.65, 0) * mm, "end": v(674.65, 17.46) * mm});
            skLineSegment(sketch, "E168", {"start": v(674.65, 17.46) * mm, "end": v(700.05, 17.46) * mm});
            skLineSegment(sketch, "E169", {"start": v(700.05, 17.46) * mm, "end": v(700.05, 19.05) * mm});
            skLineSegment(sketch, "E170", {"start": v(700.05, 19.05) * mm, "end": v(639.73, 19.05) * mm});
            skSolve(sketch);
        }
        {
            var Q0;
            Q0 = qSketchRegion(id + "F6", true);
            extrude(context, id + "F7", {"entities" : qUnion([Q0]), "operationType" : NewBodyOperationType.REMOVE, "endBound" : BoundingType.THROUGH_ALL, "oppositeDirection" : true, "depth" : 25.4 * mm});
        }
        {
            var Q0;
            Q0=makeQuery(id+"F1.opExtrude","SWEPT_FACE",FACE,{"disambiguationData":[OSD([sQuery(id+"F0.wireOp",EDGE,"E91.MirrorCS")])]});
            var sketch = newSketch(context, id + "F8", { "sketchPlane" : qUnion([Q0])});
            skLineSegment(sketch, "E171", {"start": v(1202.2, 19.05) * mm, "end": v(1202.2, 17.46) * mm});
            skLineSegment(sketch, "E172", {"start": v(1202.2, 17.46) * mm, "end": v(1176.8, 17.46) * mm});
            skLineSegment(sketch, "E173", {"start": v(1176.8, 17.46) * mm, "end": v(1176.8, 0) * mm});
            skLineSegment(sketch, "E174", {"start": v(1176.8, 0) * mm, "end": v(1167.27, 0) * mm});
            skLineSegment(sketch, "E175", {"start": v(1167.27, 0) * mm, "end": v(1167.27, 17.46) * mm});
            skLineSegment(sketch, "E176", {"start": v(1167.27, 17.46) * mm, "end": v(1141.87, 17.46) * mm});
            skLineSegment(sketch, "E177", {"start": v(1141.87, 17.46) * mm, "end": v(1141.87, 19.05) * mm});
            skLineSegment(sketch, "E178", {"start": v(1141.87, 19.05) * mm, "end": v(1202.2, 19.05) * mm});
            skSolve(sketch);
        }
        {
            var Q0;
            Q0 = qSketchRegion(id + "F8", true);
            extrude(context, id + "F9", {"entities" : qUnion([Q0]), "operationType" : NewBodyOperationType.REMOVE, "endBound" : BoundingType.THROUGH_ALL, "oppositeDirection" : true, "depth" : 25.4 * mm});
        }
        {
            var Q0;
            Q0=makeQuery(id+"F1.opExtrude","SWEPT_FACE",FACE,{"disambiguationData":[OSD([sQuery(id+"F0.wireOp",EDGE,"E83.MirrorCS")])]});
            var sketch = newSketch(context, id + "F10", { "sketchPlane" : qUnion([Q0])});
            skLineSegment(sketch, "E179.bottom", {"start": v(1518.59, 19.05) * mm, "end": v(1534.46, 19.05) * mm});
            skLineSegment(sketch, "E179.top", {"start": v(1518.59, 12.7) * mm, "end": v(1534.46, 12.7) * mm});
            skLineSegment(sketch, "E179.left", {"start": v(1518.59, 19.05) * mm, "end": v(1518.59, 12.7) * mm});
            skLineSegment(sketch, "E179.right", {"start": v(1534.46, 19.05) * mm, "end": v(1534.46, 12.7) * mm});
            skSolve(sketch);
        }
        {
            var Q0;
            Q0 = qSketchRegion(id + "F10", true);
            extrude(context, id + "F11", {"entities" : qUnion([Q0]), "operationType" : NewBodyOperationType.REMOVE, "endBound" : BoundingType.THROUGH_ALL, "oppositeDirection" : true, "depth" : 25.4 * mm});
        }
        {
            var Q0;
            Q0=makeQuery(id+"F1.opExtrude","CAP_FACE",FACE,{"disambiguationData":[OSD([sQuery(id+"F0.wireOp",EDGE,"E92.bottom"),sQuery(id+"F0.wireOp",EDGE,"E92.top"),sQuery(id+"F0.wireOp",EDGE,"E92.left"),sQuery(id+"F0.wireOp",EDGE,"E92.right"),sQuery(id+"F0.wireOp",EDGE,"E93")])],"isStart":false});
            var sketch = newSketch(context, id + "F12", { "sketchPlane" : qUnion([Q0])});
            skCircle(sketch, "E180", {"center": v(3073.24, -1241.68) * mm, "radius": 6.35 * mm});
            skSolve(sketch);
        }
        {
            var Q0;
            Q0 = qSketchRegion(id + "F12", true);
            extrude(context, id + "F13", {"entities" : qUnion([Q0]), "operationType" : NewBodyOperationType.REMOVE, "oppositeDirection" : true, "depth" : 6.35 * mm});
        }
        {
            var Q0;
            Q0=makeQuery(id+"F1.opExtrude","SWEPT_FACE",FACE,{"disambiguationData":[OSD([sQuery(id+"F0.wireOp",EDGE,"E95.top")])]});
            var sketch = newSketch(context, id + "F14", { "sketchPlane" : qUnion([Q0])});
            skLineSegment(sketch, "E181", {"start": v(4003.93, 0) * mm, "end": v(4022.98, 19.05) * mm});
            skLineSegment(sketch, "E182", {"start": v(4022.98, 19.05) * mm, "end": v(4003.93, 19.05) * mm});
            skLineSegment(sketch, "E183", {"start": v(4003.93, 19.05) * mm, "end": v(4003.93, 0) * mm});
            skLineSegment(sketch, "E184", {"start": v(4067.43, 19.05) * mm, "end": v(4067.43, 0) * mm, "construction": true});
            skLineSegment(sketch, "E185.MirrorCS", {"start": v(4130.93, 0) * mm, "end": v(4111.88, 19.05) * mm});
            skLineSegment(sketch, "E186.MirrorCS", {"start": v(4111.88, 19.05) * mm, "end": v(4130.93, 19.05) * mm});
            skLineSegment(sketch, "E187.MirrorCS", {"start": v(4130.93, 19.05) * mm, "end": v(4130.93, 0) * mm});
            skSolve(sketch);
        }
        {
            var Q0;
            Q0 = qSketchRegion(id + "F14", true);
            extrude(context, id + "F15", {"entities" : qUnion([Q0]), "operationType" : NewBodyOperationType.REMOVE, "endBound" : BoundingType.THROUGH_ALL, "oppositeDirection" : true, "depth" : 25.4 * mm});
        }
        {
            var Q0;
            Q0=makeQuery(id+"F1.opExtrude","CAP_FACE",FACE,{"disambiguationData":[OSD([sQuery(id+"F0.wireOp",EDGE,"E97.bottom"),sQuery(id+"F0.wireOp",EDGE,"E97.top"),sQuery(id+"F0.wireOp",EDGE,"E97.left"),sQuery(id+"F0.wireOp",EDGE,"E97.right"),sQuery(id+"F0.wireOp",EDGE,"E117"),sQuery(id+"F0.wireOp",EDGE,"E125"),sQuery(id+"F0.wireOp",EDGE,"E126")])],"isStart":false});
            var sketch = newSketch(context, id + "F16", { "sketchPlane" : qUnion([Q0])});
            skLineSegment(sketch, "E188.bottom", {"start": v(4654.28, -294.34) * mm, "end": v(4651.1, -294.34) * mm});
            skLineSegment(sketch, "E188.top", {"start": v(4654.28, -541.99) * mm, "end": v(4651.1, -541.99) * mm});
            skLineSegment(sketch, "E188.left", {"start": v(4654.28, -294.34) * mm, "end": v(4654.28, -541.99) * mm});
            skLineSegment(sketch, "E188.right", {"start": v(4651.1, -294.34) * mm, "end": v(4651.1, -541.99) * mm});
            skCircle(sketch, "E189", {"center": v(4590.78, -383.24) * mm, "radius": 6.35 * mm});
            skCircle(sketch, "E190", {"center": v(4590.78, -472.14) * mm, "radius": 6.35 * mm});
            skSolve(sketch);
        }
        {
            var Q0;
            Q0 = qSketchRegion(id + "F16", true);
            extrude(context, id + "F17", {"entities" : qUnion([Q0]), "operationType" : NewBodyOperationType.REMOVE, "oppositeDirection" : true, "depth" : 6.35 * mm});
        }
        {
            var Q0;
            Q0=makeQuery(id+"F1.opExtrude","SWEPT_FACE",FACE,{"disambiguationData":[OSD([sQuery(id+"F0.wireOp",EDGE,"E97.left")])]});
            var sketch = newSketch(context, id + "F18", { "sketchPlane" : qUnion([Q0])});
            skLineSegment(sketch, "E191", {"start": v(541.99, 19.05) * mm, "end": v(522.94, 0) * mm});
            skLineSegment(sketch, "E192", {"start": v(522.94, 0) * mm, "end": v(541.99, 0) * mm});
            skLineSegment(sketch, "E193", {"start": v(541.99, 0) * mm, "end": v(541.99, 19.05) * mm});
            skSolve(sketch);
        }
        {
            var Q0;
            Q0 = qSketchRegion(id + "F18", true);
            extrude(context, id + "F19", {"entities" : qUnion([Q0]), "operationType" : NewBodyOperationType.REMOVE, "endBound" : BoundingType.THROUGH_ALL, "oppositeDirection" : true, "depth" : 25.4 * mm});
        }
        {
            var Q0;
            Q0=makeQuery(id+"F1.opExtrude","CAP_FACE",FACE,{"disambiguationData":[OSD([sQuery(id+"F0.wireOp",EDGE,"E127.MirrorCS"),sQuery(id+"F0.wireOp",EDGE,"E128.MirrorCS"),sQuery(id+"F0.wireOp",EDGE,"E129.MirrorC"),sQuery(id+"F0.wireOp",EDGE,"E130.MirrorC"),sQuery(id+"F0.wireOp",EDGE,"E132.MirrorCS"),sQuery(id+"F0.wireOp",EDGE,"E133.MirrorCS"),sQuery(id+"F0.wireOp",EDGE,"E134.MirrorCS")])],"isStart":false});
            var sketch = newSketch(context, id + "F20", { "sketchPlane" : qUnion([Q0])});
            skLineSegment(sketch, "E194.bottom", {"start": v(4654.28, -802.34) * mm, "end": v(4651.1, -802.34) * mm});
            skLineSegment(sketch, "E194.top", {"start": v(4654.28, -554.69) * mm, "end": v(4651.1, -554.69) * mm});
            skLineSegment(sketch, "E194.left", {"start": v(4654.28, -802.34) * mm, "end": v(4654.28, -554.69) * mm});
            skLineSegment(sketch, "E194.right", {"start": v(4651.1, -802.34) * mm, "end": v(4651.1, -554.69) * mm});
            skCircle(sketch, "E195", {"center": v(4590.78, -624.54) * mm, "radius": 6.35 * mm});
            skCircle(sketch, "E196", {"center": v(4590.78, -713.44) * mm, "radius": 6.35 * mm});
            skSolve(sketch);
        }
        {
            var Q0;
            Q0 = qSketchRegion(id + "F20", true);
            extrude(context, id + "F21", {"entities" : qUnion([Q0]), "operationType" : NewBodyOperationType.REMOVE, "oppositeDirection" : true, "depth" : 6.35 * mm});
        }
        {
            var Q0;
            Q0=makeQuery(id+"F1.opExtrude","SWEPT_FACE",FACE,{"disambiguationData":[OSD([sQuery(id+"F0.wireOp",EDGE,"E133.MirrorCS")])]});
            var sketch = newSketch(context, id + "F22", { "sketchPlane" : qUnion([Q0])});
            skLineSegment(sketch, "E197", {"start": v(554.69, 0) * mm, "end": v(573.74, 0) * mm});
            skLineSegment(sketch, "E198", {"start": v(573.74, 0) * mm, "end": v(554.69, 19.05) * mm});
            skLineSegment(sketch, "E199", {"start": v(554.69, 19.05) * mm, "end": v(554.69, 0) * mm});
            skSolve(sketch);
        }
        {
            var Q0;
            Q0 = qSketchRegion(id + "F22", true);
            extrude(context, id + "F23", {"entities" : qUnion([Q0]), "operationType" : NewBodyOperationType.REMOVE, "endBound" : BoundingType.THROUGH_ALL, "oppositeDirection" : true, "depth" : 25.4 * mm});
        }
        {
            var Q0;
            Q0=makeQuery(id+"F1.opExtrude","SWEPT_FACE",FACE,{"disambiguationData":[OSD([sQuery(id+"F0.wireOp",EDGE,"E98.top")])]});
            var sketch = newSketch(context, id + "F24", { "sketchPlane" : qUnion([Q0])});
            skLineSegment(sketch, "E200", {"start": v(3787.6, 9.53) * mm, "end": v(3778.08, 0) * mm});
            skLineSegment(sketch, "E201", {"start": v(3778.08, 0) * mm, "end": v(3787.6, 0) * mm});
            skLineSegment(sketch, "E202", {"start": v(3787.6, 0) * mm, "end": v(3787.6, 9.53) * mm});
            skSolve(sketch);
        }
        {
            var Q0;
            Q0 = qSketchRegion(id + "F24", true);
            extrude(context, id + "F25", {"entities" : qUnion([Q0]), "operationType" : NewBodyOperationType.REMOVE, "endBound" : BoundingType.THROUGH_ALL, "oppositeDirection" : true, "depth" : 25.4 * mm});
        }
        {
            var Q0;
            Q0=makeQuery(id+"F1.opExtrude","CAP_FACE",FACE,{"disambiguationData":[OSD([sQuery(id+"F0.wireOp",EDGE,"E100.bottom"),sQuery(id+"F0.wireOp",EDGE,"E100.top"),sQuery(id+"F0.wireOp",EDGE,"E100.left"),sQuery(id+"F0.wireOp",EDGE,"E100.right"),sQuery(id+"F0.wireOp",EDGE,"E140.0.startCap"),sQuery(id+"F0.wireOp",EDGE,"E140.0.endCap"),sQuery(id+"F0.wireOp",EDGE,"E140.0.left"),sQuery(id+"F0.wireOp",EDGE,"E140.0.right"),sQuery(id+"F0.wireOp",EDGE,"E141.MirrorCS"),sQuery(id+"F0.wireOp",EDGE,"E142.MirrorCS"),sQuery(id+"F0.wireOp",EDGE,"E145.MirrorCS"),sQuery(id+"F0.wireOp",EDGE,"E146.MirrorCS")])],"isStart":false});
            var sketch = newSketch(context, id + "F26", { "sketchPlane" : qUnion([Q0])});
            skLineSegment(sketch, "E203", {"start": v(4118.5, -1309.3) * mm, "end": v(4207.4, -1309.3) * mm, "construction": true});
            skLineSegment(sketch, "E204.0", {"start": v(4152.47, -1169.6) * mm, "end": v(4173.41, -1169.6) * mm});
            skArc(sketch, "E204.1", {"start": v(4152.47, -1188.65) * mm, "mid": v(4142.95, -1179.13) * mm, "end": v(4152.47, -1169.6) * mm});
            skLineSegment(sketch, "E204.2", {"start": v(4152.47, -1188.65) * mm, "end": v(4173.41, -1188.65) * mm});
            skArc(sketch, "E204.3", {"start": v(4173.41, -1169.6) * mm, "mid": v(4182.94, -1179.13) * mm, "end": v(4173.41, -1188.65) * mm});
            skLineSegment(sketch, "E205.MirrorCS", {"start": v(4152.47, -1429.95) * mm, "end": v(4173.41, -1429.95) * mm});
            skArc(sketch, "E206.MirrorCS", {"start": v(4173.41, -1449) * mm, "mid": v(4182.94, -1439.48) * mm, "end": v(4173.41, -1429.95) * mm});
            skArc(sketch, "E207.MirrorCS", {"start": v(4152.47, -1429.95) * mm, "mid": v(4142.95, -1439.48) * mm, "end": v(4152.47, -1449) * mm});
            skLineSegment(sketch, "E208.MirrorCS", {"start": v(4152.47, -1449) * mm, "end": v(4173.41, -1449) * mm});
            skSolve(sketch);
        }
        {
            var Q0;
            Q0 = qSketchRegion(id + "F26", true);
            extrude(context, id + "F27", {"entities" : qUnion([Q0]), "operationType" : NewBodyOperationType.REMOVE, "oppositeDirection" : true, "depth" : 6.35 * mm});
        }
        {
            var Q0;
            Q0=makeQuery(id+"F1.opExtrude","CAP_FACE",FACE,{"disambiguationData":[OSD([sQuery(id+"F0.wireOp",EDGE,"E104"),sQuery(id+"F0.wireOp",EDGE,"E147")])],"isStart":false});
            var sketch = newSketch(context, id + "F28", { "sketchPlane" : qUnion([Q0])});
            skCircle(sketch, "E209", {"center": v(4318.4, -1993.53) * mm, "radius": 5.56 * mm});
            skSolve(sketch);
        }
        {
            var Q0;
            Q0 = qSketchRegion(id + "F28", true);
            extrude(context, id + "F29", {"entities" : qUnion([Q0]), "operationType" : NewBodyOperationType.REMOVE, "oppositeDirection" : true, "depth" : 6.35 * mm});
        }
        {
            var Q0;
            Q0=makeQuery(id+"F1.opExtrude","SWEPT_FACE",FACE,{"disambiguationData":[OSD([sQuery(id+"F0.wireOp",EDGE,"E150")])]});
            var sketch = newSketch(context, id + "F30", { "sketchPlane" : qUnion([Q0])});
            skCircle(sketch, "E210", {"center": v(3893.95, 9.53) * mm, "radius": 3.97 * mm});
            skPoint(sketch, "E210.centerSnap0", {"position": v(3881.25, 9.53) * mm});
            skSolve(sketch);
        }
        {
            var Q0;
            Q0 = qSketchRegion(id + "F30", true);
            extrude(context, id + "F31", {"entities" : qUnion([Q0]), "operationType" : NewBodyOperationType.REMOVE, "endBound" : BoundingType.THROUGH_ALL, "oppositeDirection" : true, "depth" : 25.4 * mm});
        }
        {
            var Q0;
            Q0=makeQuery(id+"F1.opExtrude","SWEPT_FACE",FACE,{"disambiguationData":[OSD([sQuery(id+"F0.wireOp",EDGE,"E102.top")])]});
            var sketch = newSketch(context, id + "F32", { "sketchPlane" : qUnion([Q0])});
            skLineSegment(sketch, "E211.bottom", {"start": v(3956.65, 0) * mm, "end": v(3948.71, 0) * mm});
            skLineSegment(sketch, "E211.top", {"start": v(3956.65, 4.76) * mm, "end": v(3948.71, 4.76) * mm});
            skLineSegment(sketch, "E211.left", {"start": v(3956.65, 0) * mm, "end": v(3956.65, 4.76) * mm});
            skLineSegment(sketch, "E211.right", {"start": v(3948.71, 0) * mm, "end": v(3948.71, 4.76) * mm});
            skLineSegment(sketch, "E212", {"start": v(3952.68, 4.76) * mm, "end": v(3952.68, 0) * mm, "construction": true});
            skSolve(sketch);
        }
        {
            var Q0;
            Q0 = qSketchRegion(id + "F32", true);
            extrude(context, id + "F33", {"entities" : qUnion([Q0]), "operationType" : NewBodyOperationType.REMOVE, "endBound" : BoundingType.THROUGH_ALL, "oppositeDirection" : true, "depth" : 25.4 * mm});
        }
    });
